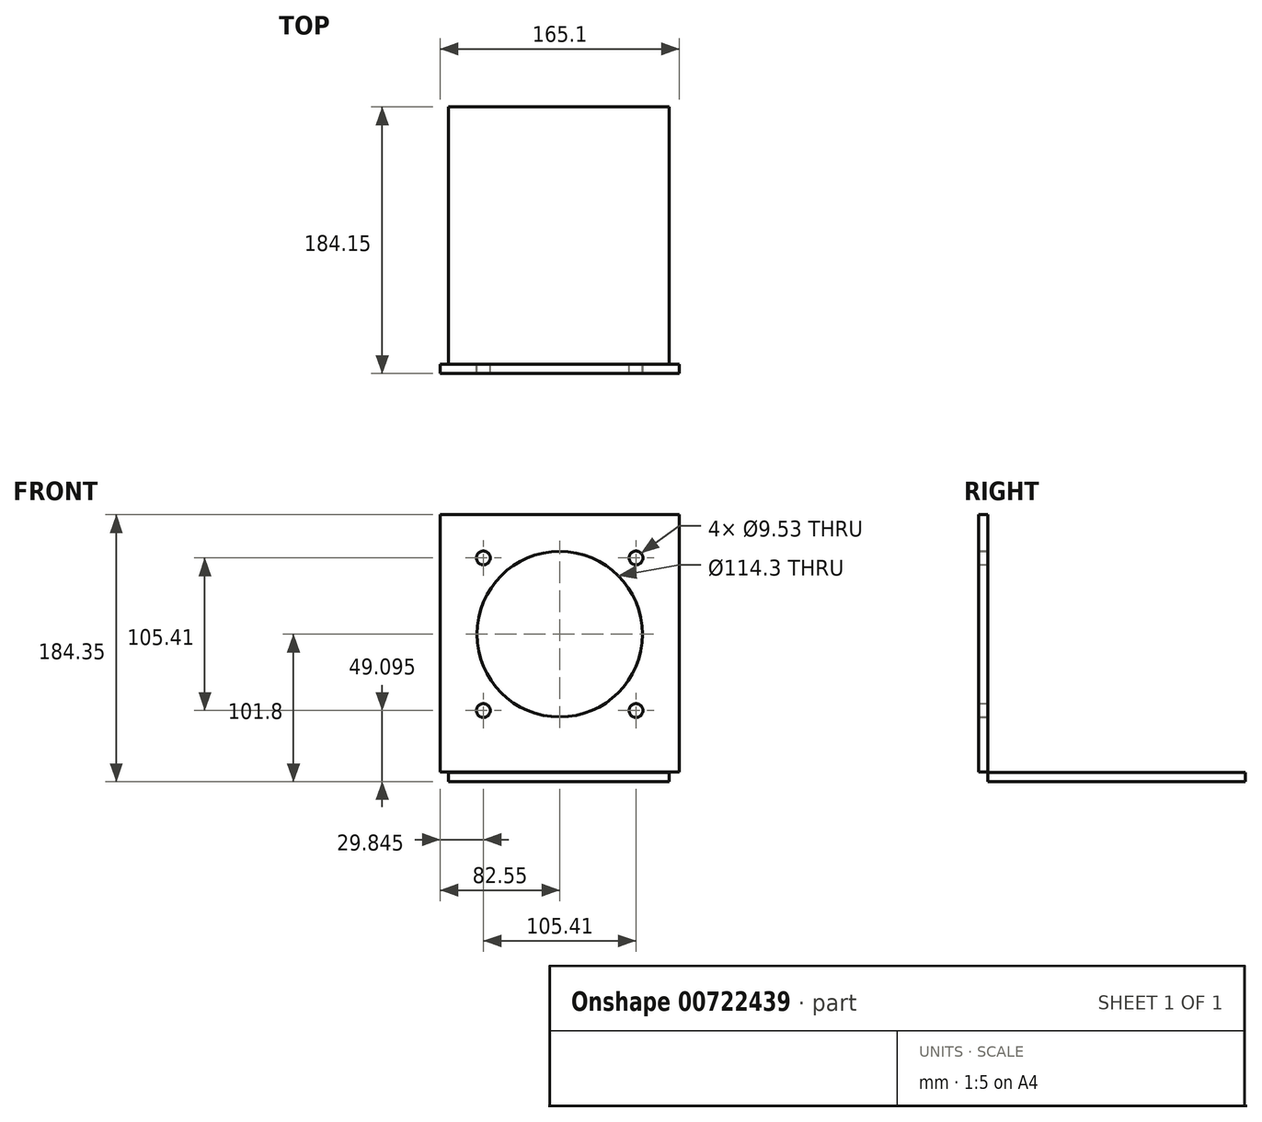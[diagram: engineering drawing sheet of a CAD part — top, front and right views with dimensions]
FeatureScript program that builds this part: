
annotation { "Feature Type Name" : "Feature", "Feature Type Description" : "" }
export const myFeature = defineFeature(function(context is Context, id is Id, definition is map)
    precondition{}
    {
        {
            var Q0;
            Q0=qCreatedBy(makeId("Front.planeOp"),FACE);
            var sketch = newSketch(context, id + "F0", { "sketchPlane" : qUnion([Q0])});
            skLineSegment(sketch, "E0.bottom", {"start": v(82.55, 88.9) * mm, "end": v(-82.55, 88.9) * mm});
            skLineSegment(sketch, "E0.top", {"start": v(82.55, -88.9) * mm, "end": v(-82.55, -88.9) * mm});
            skLineSegment(sketch, "E0.left", {"start": v(82.55, 88.9) * mm, "end": v(82.55, -88.9) * mm});
            skLineSegment(sketch, "E0.right", {"start": v(-82.55, 88.9) * mm, "end": v(-82.55, -88.9) * mm});
            skPoint(sketch, "E0.middle", {"position": v(0, 0) * mm});
            skLineSegment(sketch, "E1", {"start": v(-82.55, -88.9) * mm, "end": v(-82.55, -76.2) * mm});
            skPoint(sketch, "E2.middle", {"position": v(0, 6.35) * mm});
            skCircle(sketch, "E3", {"center": v(-52.7, 59.06) * mm, "radius": 4.76 * mm});
            skCircle(sketch, "E4", {"center": v(52.7, 59.06) * mm, "radius": 4.76 * mm});
            skCircle(sketch, "E5", {"center": v(52.7, -46.36) * mm, "radius": 4.76 * mm});
            skCircle(sketch, "E6", {"center": v(-52.7, -46.36) * mm, "radius": 4.76 * mm});
            skCircle(sketch, "E7", {"center": v(0, 6.35) * mm, "radius": 57.15 * mm});
            skLineSegment(sketch, "E8", {"start": v(-82.55, -88.9) * mm, "end": v(-76.2, -88.9) * mm, "construction": true});
            skLineSegment(sketch, "E9", {"start": v(-76.2, -88.9) * mm, "end": v(-76.2, -111.03) * mm, "construction": true});
            skSolve(sketch);
        }
        {
            var Q0;
            {var subQ0=sQuery(id+"F0.wireOp",EDGE,"E0.top");Q0=makeQuery(id+"F0.imprint","IMPRINT",FACE,{"disambiguationData":[TD([[makeQuery(id+"F0.imprint","IMPRINT",EDGE,{"derivedFrom":subQ0}),-1.0]])]});}
            var Q1;
            {var subQ0=sQuery(id+"F0.wireOp",EDGE,"Qb17fNjA-IIBl-hS5k-5iVL-ygz58cl4BNyp");var subQ1=sQuery(id+"F0.wireOp",EDGE,"E0.left");var subQ2=makeQuery(id+"F0.imprint","INTERSECT",VERTEX,{"derivedFrom":[sQuery(id+"F0.wireOp",EDGE,"E0.bottom"),subQ1,subQ0]});Q1=makeQuery(id+"F0.imprint","IMPRINT",FACE,{"disambiguationData":[TD([[makeQuery(id+"F0.imprint","IMPRINT",EDGE,{"disambiguationData":[TD([[subQ2,-1.0]])],"derivedFrom":subQ1}),-1.0]])]});}
            var Q2;
            {var subQ0=sQuery(id+"F0.wireOp",EDGE,"E0.right");Q2=makeQuery(id+"F0.imprint","IMPRINT",FACE,{"disambiguationData":[TD([[makeQuery(id+"F0.imprint","IMPRINT",EDGE,{"derivedFrom":subQ0}),1.0]])]});}
            var Q3;
            {var subQ0=sQuery(id+"F0.wireOp",EDGE,"GgyLbU7E-cmOZ-eF8M-adwv-XId522wLtesK");Q3=makeQuery(id+"F0.imprint","IMPRINT",FACE,{"disambiguationData":[TD([[makeQuery(id+"F0.imprint","IMPRINT",EDGE,{"derivedFrom":subQ0}),1.0]])]});}
            var Q4;
            {var subQ0=sQuery(id+"F0.wireOp",EDGE,"E0.bottom");Q4=makeQuery(id+"F0.imprint","IMPRINT",FACE,{"disambiguationData":[TD([[makeQuery(id+"F0.imprint","IMPRINT",EDGE,{"derivedFrom":subQ0}),1.0]])]});}
            extrude(context, id + "F1", {"entities" : qUnion([Q0, Q1, Q2, Q3, Q4]), "depth" : 6.35 * mm, "offsetDistance" : 25.4 * mm});
        }
        {
            var Q0;
            Q0=makeQuery(id+"F1.opExtrude","CAP_FACE",FACE,{"disambiguationData":[OSD([sQuery(id+"F0.wireOp",EDGE,"E0.bottom"),sQuery(id+"F0.wireOp",EDGE,"E0.top"),sQuery(id+"F0.wireOp",EDGE,"E0.left"),sQuery(id+"F0.wireOp",EDGE,"E0.right"),sQuery(id+"F0.wireOp",EDGE,"E1"),sQuery(id+"F0.wireOp",EDGE,"UY4sjrBE-H1Fr-LbOf-XKTV-cUZykeqfdQaL")])],"isStart":false});
            var sketch = newSketch(context, id + "F2", { "sketchPlane" : qUnion([Q0])});
            skLineSegment(sketch, "E10", {"start": v(0, 80.89) * mm, "end": v(0, -68.19) * mm, "construction": true});
            skLineSegment(sketch, "E11", {"start": v(0, -68.19) * mm, "end": v(0, 6.35) * mm, "construction": true});
            skLineSegment(sketch, "E12", {"start": v(0, 6.35) * mm, "end": v(-74.54, 6.35) * mm, "construction": true});
            skLineSegment(sketch, "E13", {"start": v(-74.54, 6.35) * mm, "end": v(74.54, 6.35) * mm, "construction": true});
            skCircle(sketch, "E14", {"center": v(0, 6.35) * mm, "radius": 57.15 * mm});
            skCircle(sketch, "E15", {"center": v(-52.63, 59.13) * mm, "radius": 4.76 * mm});
            skCircle(sketch, "E16", {"center": v(52.7, 59.06) * mm, "radius": 4.76 * mm});
            skCircle(sketch, "E17", {"center": v(-53.01, -46.05) * mm, "radius": 4.76 * mm});
            skCircle(sketch, "E18", {"center": v(52.7, -46.36) * mm, "radius": 4.76 * mm});
            skSolve(sketch);
        }
        {
            var Q0;
            Q0 = qSketchRegion(id + "F0", true);
            extrude(context, id + "F3", {"entities" : qUnion([Q0]), "operationType" : NewBodyOperationType.ADD, "depth" : 6.35 * mm, "offsetDistance" : 25.4 * mm});
        }
        {
            var Q0;
            Q0=makeQuery(id+"F2.imprint","IMPRINT",FACE,{"disambiguationData":[TD([[makeQuery(id+"F2.imprint","IMPRINT",EDGE,{"derivedFrom":sQuery(id+"F2.wireOp",EDGE,"E14")}),-1.0]])]});
            var sketch = newSketch(context, id + "F4", { "sketchPlane" : qUnion([Q0])});
            skLineSegment(sketch, "E19.bottom", {"start": v(-76.89, -111.46) * mm, "end": v(75.51, -111.46) * mm});
            skLineSegment(sketch, "E19.top", {"start": v(-76.89, -117.8) * mm, "end": v(75.51, -117.8) * mm});
            skLineSegment(sketch, "E19.left", {"start": v(-76.89, -111.46) * mm, "end": v(-76.89, -117.8) * mm});
            skLineSegment(sketch, "E19.right", {"start": v(75.51, -111.46) * mm, "end": v(75.51, -117.8) * mm});
            skSolve(sketch);
        }
        {
            var Q0;
            Q0=makeQuery(id+"F4.imprint","IMPRINT",FACE,{"disambiguationData":[TD([[makeQuery(id+"F4.imprint","IMPRINT",EDGE,{"derivedFrom":sQuery(id+"F4.wireOp",EDGE,"E19.bottom")}),-1.0]])]});
            extrude(context, id + "F5", {"entities" : qUnion([Q0]), "oppositeDirection" : true, "depth" : 177.8 * mm, "offsetDistance" : 25.4 * mm});
        }
        {
            var Q0;
            Q0=makeQuery(id+"F5.opExtrude","SWEPT_BODY",BODY,{"disambiguationData":[OSD([sQuery(id+"F4.wireOp",EDGE,"E19.bottom"),sQuery(id+"F4.wireOp",EDGE,"E19.top"),sQuery(id+"F4.wireOp",EDGE,"E19.left"),sQuery(id+"F4.wireOp",EDGE,"E19.right")])]});
            transform(context, id + "F6", {"entities" : qUnion([Q0]), "transformType" : TransformType.TRANSLATION_3D, "dx" : 0 * mm, "dy" : 6.35 * mm, "dz" : 22.35 * mm, "makeCopy" : false});
        }
    });
